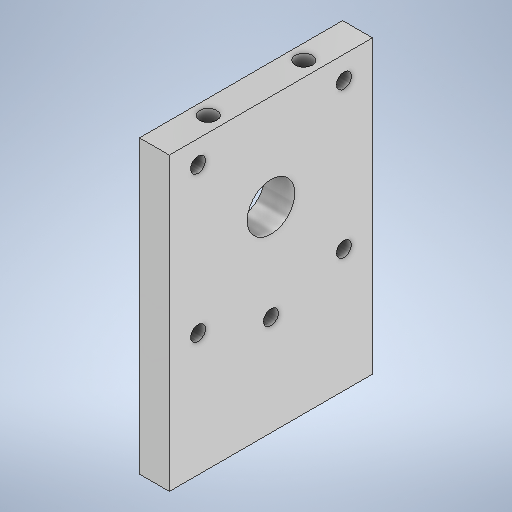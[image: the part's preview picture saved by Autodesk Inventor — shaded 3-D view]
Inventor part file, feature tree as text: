
AUTODESK INVENTOR PART (.ipt)
format: ipt  version: 2025.1 (Build 291241020, 241B)  size: 297,984 bytes
history: native  units: in
note: dims shown in document units (in); Inventor stores cm internally (conversion verified against a paired STEP export)
features: sketch x8, extrude x7, hole x1, projected_geometry x1
ambient origin geometry x8: Origin, YZ Plane, XZ Plane, XY Plane, X Axis, Y Axis, Z Axis, Center Point
bodies: Solid1 (feature_tree)
feature tree (17):
  extrude  "Extrusion1"  Depth=2.5in
  extrude  "Extrusion2"  Depth=0.0625in
  extrude  "Extrusion3"  Depth=0.0625in
  extrude  "Extrusion4"  Depth=0.3976in
  extrude  "Extrusion5"  TaperAngle=0.0deg  [1 undecoded]
  extrude  "Extrusion6"  Depth=0.8in
  extrude  "Extrusion7"  Depth=0.6in
  hole  "Hole1"  [1 undecoded]
  sketch  "Sketch1"  dims[d0=11.0in d1=2.5in]
  sketch  "Sketch2"  dims[d2=1.7in d3=0.0in d4=0.0625in]
  sketch  "Sketch3"  dims[d5=0.0625in d6=0.0625in]
  sketch  "Sketch4"  dims[d7=1.5in d8=0.0in d9=0.3976in]
  sketch  "Sketch5"  dims[d10=0.8in d11=0.0in d12=0.0in]
  sketch  "Sketch6"  dims[d13=0.125in d15=0.8in]
  sketch  "Sketch7"  dims[d16=0.4in d17=0.6in]
  projected_geometry  "Projected Loop1"
  sketch  "Sketch8"  dims[d18=0.1875in d19=1.0in d20=0.0in d21=0.125in d22=0.6102in d23=0.6102in d24=1.0in d25=0.0in d26=0.0in d27=0.0in d28=0.25in d29=0.0in d30=0.45in d31=0.45in d32=0.144in d33=0.75in d34=0.375in d35=0.25in d36=0.5635in d37=0.885in d38=0.8108in d39=0.75in d40=0.8108in d41=0.0625in d42=0.75in d43=0.375in]
note: 2 required parameter values undecoded (feature->parameter linkage not recoverable at this tier; creation-order binding heuristic only, values carry confidence <= 0.55)
